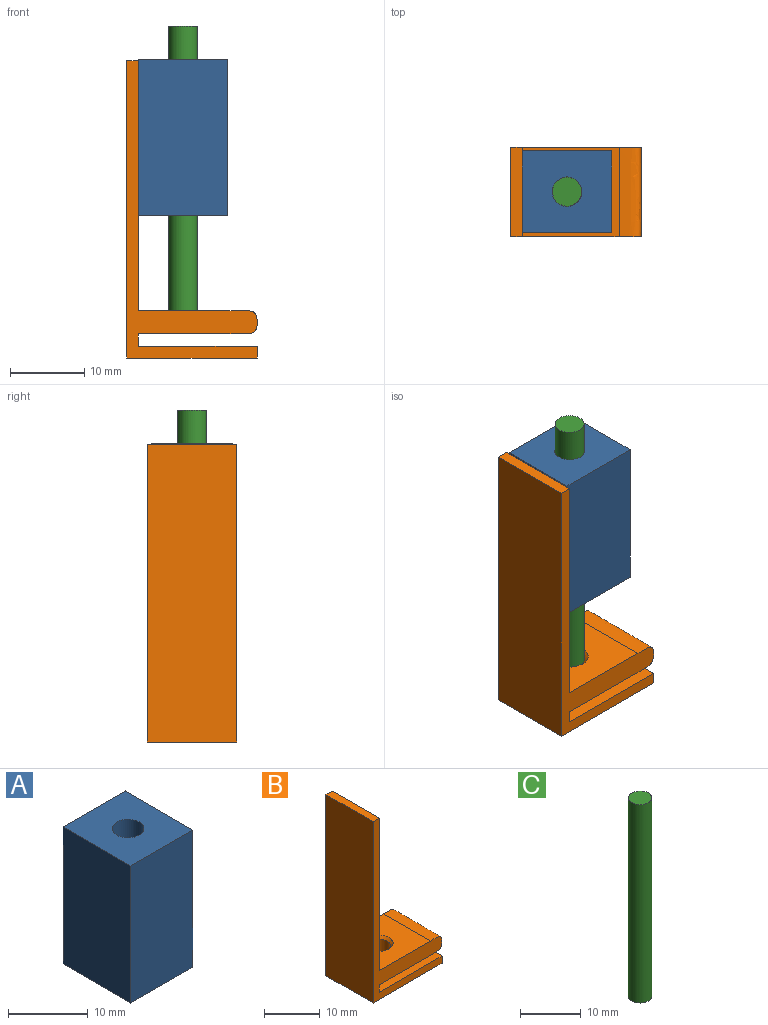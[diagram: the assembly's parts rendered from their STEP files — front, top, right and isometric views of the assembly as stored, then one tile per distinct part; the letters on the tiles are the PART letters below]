
ASSEMBLY  parts=3 mates=2
PART A: 7 faces, bbox 11x12x21 mm
  f0: plane 21x11mm, normal (0,-1,0), area 231mm2, adj f1,f4,f5,f6
  f1: plane 21x12mm, normal (1,0,0), area 252mm2, adj f0,f2,f5,f6
  f2: plane 21x11mm, normal (0,1,0), area 231mm2, adj f1,f4,f5,f6
  f3: cylinder r=2mm len=21mm, axis (0,0,-1), area 263.9mm2, adj f5,f6
  f4: plane 21x12mm, normal (-1,0,0), area 252mm2, adj f0,f2,f5,f6
  f5: plane 12x11mm, normal (0,0,1), area 119.4mm2, adj f0,f1,f2,f3,f4
  f6: plane 12x11mm, normal (0,0,-1), area 119.4mm2, adj f0,f1,f2,f3,f4
PART B: 15 faces, bbox 18.2x13.9x40.7 mm
  f0: plane 13x12mm, normal (0,0,1), area 136.4mm2, adj f1,f9,f10,f12,f14
  f1: plane 33.61x12mm, normal (1,0,0), area 403.3mm2, adj f0,f2,f9,f10
  f2: plane 12x1.58mm, normal (0,0,1), area 18.9mm2, adj f1,f3,f9,f10
  f3: plane 40x12mm, normal (-1,0,0), area 480mm2, adj f2,f4,f9,f10
  f4: plane 17.57x12mm, normal (0,0,-1), area 210.9mm2, adj f3,f5,f9,f10
  f5: plane 12x1.57mm, normal (1,0,0), area 18.9mm2, adj f4,f6,f9,f10
  f6: plane 16x12mm, normal (0,0,1), area 192mm2, adj f5,f7,f9,f10
  f7: plane 12x1.66mm, normal (1,0,0), area 20mm2, adj f6,f8,f9,f10
  f8: plane 13x12mm, normal (0,0,-1), area 143.4mm2, adj f7,f9,f10,f11,f13
  f9: plane 40.67x18.25mm, normal (0,-1,0), area 138.3mm2, adj f0,f1,f2,f3,f4,f5,f6,f7
  f10: plane 40.67x18.25mm, normal (0,1,0), area 138.3mm2, adj f0,f1,f2,f3,f4,f5,f6,f7
  f11: cylinder r=2mm len=4mm, axis (0,0,1), area 33.3mm2, adj f8,f12
  f12: cone r=2mm half-angle=45deg, axis (0,0,1), area 10mm2, adj f0,f11
  f13: bspline ~13.2x3mm, area 48.3mm2, adj f8,f9,f10,f14
  f14: bspline ~13.2x3mm, area 48.3mm2, adj f0,f9,f10,f13
PART C: 3 faces, bbox 3.9x3.9x40 mm
  f0: cylinder r=1.95mm len=40mm, axis (0,0,-1), area 490.1mm2, adj f1,f2
  f1: plane 3.9x3.9mm, normal (0,0,1), area 11.9mm2, adj f0
  f2: plane 3.9x3.9mm, normal (0,0,-1), area 11.9mm2, adj f0
PLACE A rot(axis=(0,0,-1),90deg) t=(37.3,-92.53,24.46)mm
PLACE B t=(-10.42,-30.2,15.66)mm
PLACE C rot(axis=(0,0,1),56.1deg) t=(4.19,26.66,9.92)mm
MATE fastened A.f0 <-> B.f1  axis (-1,0,0) through (-16.03,-36.2,34.96)mm
MATE cylindrical C.f0 <-> A.f3  axis (0,0,1) through (-10.03,-36.2,49.92)mm
